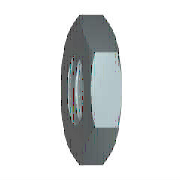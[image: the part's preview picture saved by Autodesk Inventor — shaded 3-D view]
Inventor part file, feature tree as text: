
AUTODESK INVENTOR PART (.ipt)
format: ipt  version: 2024.1 (Build 281209000, 209)  size: 162,816 bytes
history: native  units: mm (DEFAULTED — no unit token found)
features: chamfer x1, hole x1, other x1, plane x1
ambient origin geometry x7: Origin, YZ Plane, XZ Plane, X Axis, Y Axis, Z Axis, Center Point
bodies: Solid1 (feature_tree), Body (feature_tree)
feature tree (4):
  chamfer  "Chamfer1"  Distance=6.350853mm
  hole  "Thread"  [1 undecoded]
  other  "Work Axis1"
  plane  "Work Plane1"
note: 1 required parameter value undecoded (feature->parameter linkage not recoverable at this tier; creation-order binding heuristic only, values carry confidence <= 0.55)
